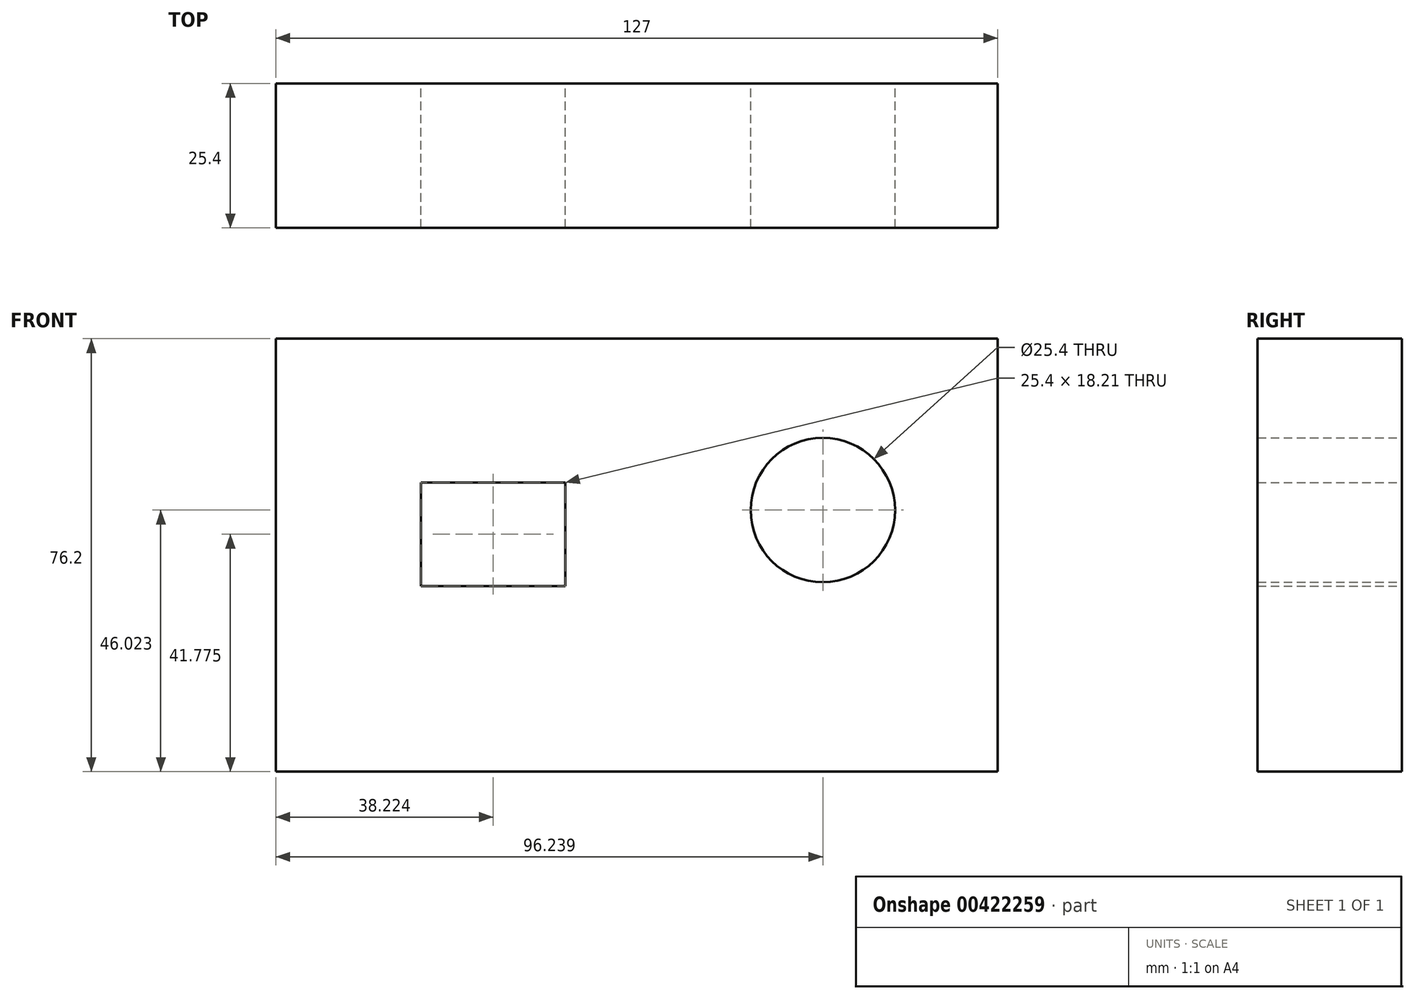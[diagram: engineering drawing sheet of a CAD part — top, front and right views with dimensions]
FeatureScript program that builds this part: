
annotation { "Feature Type Name" : "Feature", "Feature Type Description" : "" }
export const myFeature = defineFeature(function(context is Context, id is Id, definition is map)
    precondition{}
    {
        {
            var Q0;
            Q0=qCreatedBy(makeId("Front.planeOp"),FACE);
            var sketch = newSketch(context, id + "F0", { "sketchPlane" : qUnion([Q0])});
            skLineSegment(sketch, "E0.bottom", {"start": v(0, 0) * mm, "end": v(-127, 0) * mm});
            skLineSegment(sketch, "E0.top", {"start": v(0, 76.2) * mm, "end": v(-127, 76.2) * mm});
            skLineSegment(sketch, "E0.left", {"start": v(0, 0) * mm, "end": v(0, 76.2) * mm});
            skLineSegment(sketch, "E0.right", {"start": v(-127, 0) * mm, "end": v(-127, 76.2) * mm});
            skCircle(sketch, "E1", {"center": v(-30.76, 46.02) * mm, "radius": 12.7 * mm});
            skLineSegment(sketch, "E2.bottom", {"start": v(-101.48, 50.88) * mm, "end": v(-76.08, 50.88) * mm});
            skLineSegment(sketch, "E2.top", {"start": v(-101.48, 32.67) * mm, "end": v(-76.08, 32.67) * mm});
            skLineSegment(sketch, "E2.left", {"start": v(-101.48, 50.88) * mm, "end": v(-101.48, 32.67) * mm});
            skLineSegment(sketch, "E2.right", {"start": v(-76.08, 50.88) * mm, "end": v(-76.08, 32.67) * mm});
            skSolve(sketch);
        }
        {
            var Q0;
            Q0 = qSketchRegion(id + "F0", true);
            extrude(context, id + "F1", {"entities" : qUnion([Q0]), "depth" : 25.4 * mm});
        }
    });
